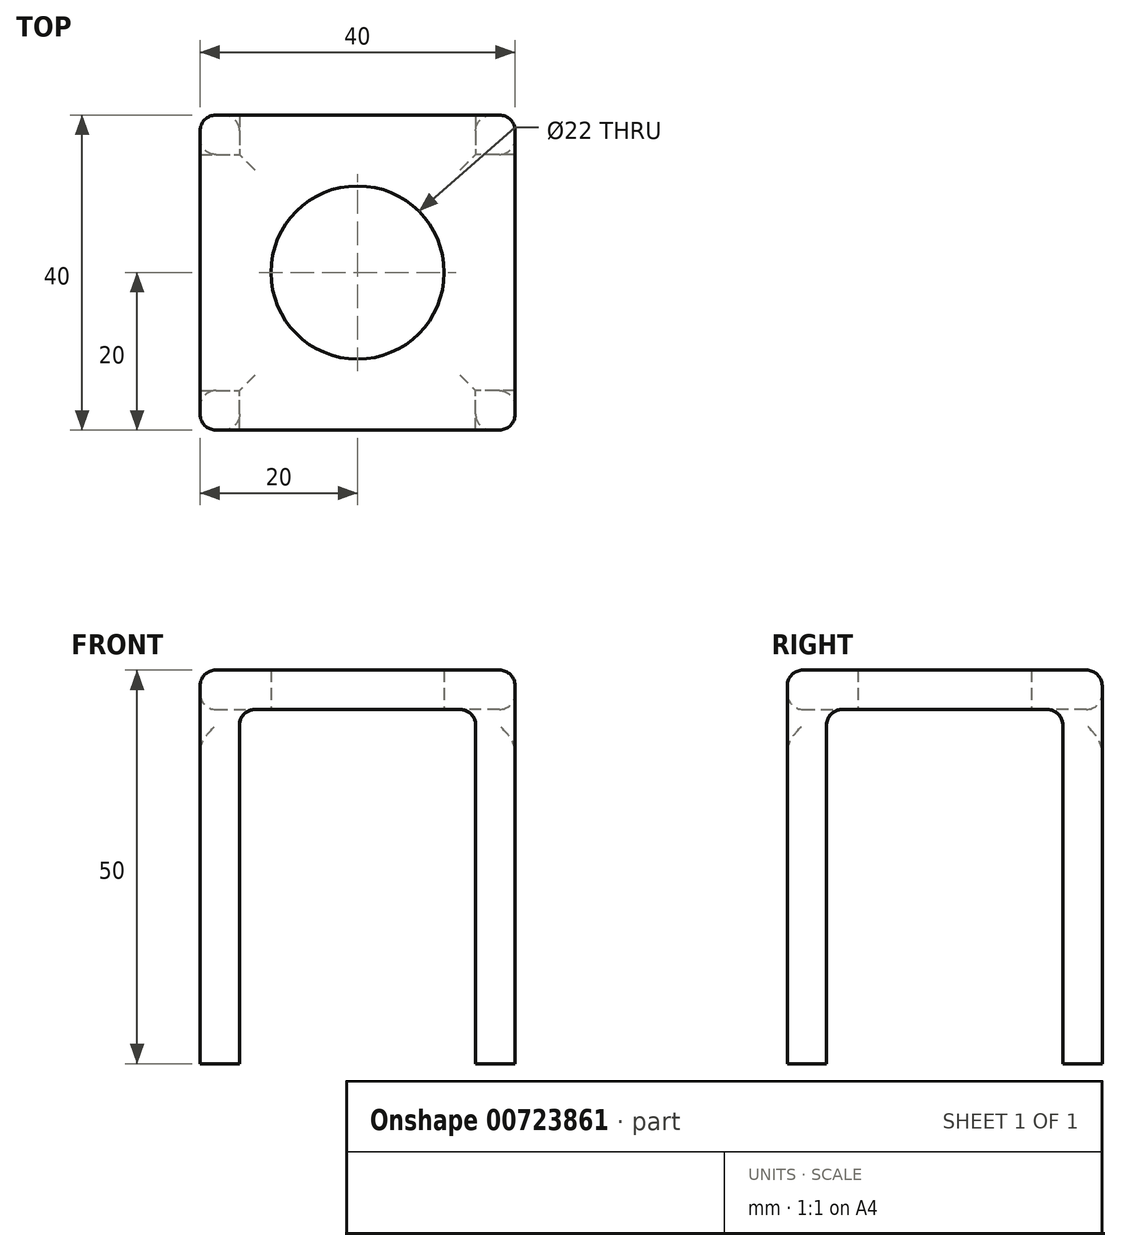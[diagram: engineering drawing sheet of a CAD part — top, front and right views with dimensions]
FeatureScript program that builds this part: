
annotation { "Feature Type Name" : "Feature", "Feature Type Description" : "" }
export const myFeature = defineFeature(function(context is Context, id is Id, definition is map)
    precondition{}
    {
        {
            var Q0;
            Q0=qCreatedBy(makeId("Top.planeOp"),FACE);
            var sketch = newSketch(context, id + "F0", { "sketchPlane" : qUnion([Q0])});
            skLineSegment(sketch, "E0.bottom", {"start": v(0, 0) * mm, "end": v(5, 0) * mm});
            skLineSegment(sketch, "E0.top", {"start": v(0, 5) * mm, "end": v(5, 5) * mm});
            skLineSegment(sketch, "E0.left", {"start": v(0, 0) * mm, "end": v(0, 5) * mm});
            skLineSegment(sketch, "E0.right", {"start": v(5, 0) * mm, "end": v(5, 5) * mm});
            skPoint(sketch, "E1", {"position": v(20, 20) * mm});
            skLineSegment(sketch, "E2.1.0", {"start": v(40, 5) * mm, "end": v(35, 5) * mm});
            skLineSegment(sketch, "E2.1.1", {"start": v(40, 0) * mm, "end": v(35, 0) * mm});
            skLineSegment(sketch, "E2.1.2", {"start": v(35, 0) * mm, "end": v(35, 5) * mm});
            skLineSegment(sketch, "E2.1.3", {"start": v(40, 0) * mm, "end": v(40, 5) * mm});
            skLineSegment(sketch, "E2.2.0", {"start": v(35, 40) * mm, "end": v(35, 35) * mm});
            skLineSegment(sketch, "E2.2.1", {"start": v(40, 40) * mm, "end": v(40, 35) * mm});
            skLineSegment(sketch, "E2.2.2", {"start": v(40, 35) * mm, "end": v(35, 35) * mm});
            skLineSegment(sketch, "E2.2.3", {"start": v(40, 40) * mm, "end": v(35, 40) * mm});
            skLineSegment(sketch, "E2.3.0", {"start": v(0, 35) * mm, "end": v(5, 35) * mm});
            skLineSegment(sketch, "E2.3.1", {"start": v(0, 40) * mm, "end": v(5, 40) * mm});
            skLineSegment(sketch, "E2.3.2", {"start": v(5, 40) * mm, "end": v(5, 35) * mm});
            skLineSegment(sketch, "E2.3.3", {"start": v(0, 40) * mm, "end": v(0, 35) * mm});
            skSolve(sketch);
        }
        {
            var Q0;
            Q0 = qSketchRegion(id + "F0", true);
            extrude(context, id + "F1", {"entities" : qUnion([Q0]), "depth" : 50 * mm, "offsetDistance" : 25 * mm});
        }
        {
            var Q0;
            Q0=makeQuery(id+"F1.opExtrude","CAP_FACE",FACE,{"disambiguationData":[OSD([sQuery(id+"F0.wireOp",EDGE,"E2.3.0"),sQuery(id+"F0.wireOp",EDGE,"E2.3.1"),sQuery(id+"F0.wireOp",EDGE,"E2.3.2"),sQuery(id+"F0.wireOp",EDGE,"E2.3.3")])],"isStart":false});
            var sketch = newSketch(context, id + "F2", { "sketchPlane" : qUnion([Q0])});
            skLineSegment(sketch, "E3.bottom", {"start": v(0, 0) * mm, "end": v(40, 0) * mm});
            skLineSegment(sketch, "E3.top", {"start": v(0, 40) * mm, "end": v(40, 40) * mm});
            skLineSegment(sketch, "E3.left", {"start": v(0, 0) * mm, "end": v(0, 40) * mm});
            skLineSegment(sketch, "E3.right", {"start": v(40, 0) * mm, "end": v(40, 40) * mm});
            skSolve(sketch);
        }
        {
            var Q0;
            Q0 = qSketchRegion(id + "F2", true);
            extrude(context, id + "F3", {"entities" : qUnion([Q0]), "operationType" : NewBodyOperationType.ADD, "oppositeDirection" : true, "depth" : 5 * mm, "offsetDistance" : 25 * mm});
        }
        {
            var Q0;
            Q0=makeQuery(id+"F3.boolean.opBoolean","MERGE",FACE,{"derivedFrom":[makeQuery(id+"F1.opExtrude","CAP_FACE",FACE,{"disambiguationData":[OSD([sQuery(id+"F0.wireOp",EDGE,"E0.bottom"),sQuery(id+"F0.wireOp",EDGE,"E0.top"),sQuery(id+"F0.wireOp",EDGE,"E0.left"),sQuery(id+"F0.wireOp",EDGE,"E0.right")])],"isStart":false}),makeQuery(id+"F1.opExtrude","CAP_FACE",FACE,{"disambiguationData":[OSD([sQuery(id+"F0.wireOp",EDGE,"E2.1.0"),sQuery(id+"F0.wireOp",EDGE,"E2.1.1"),sQuery(id+"F0.wireOp",EDGE,"E2.1.2"),sQuery(id+"F0.wireOp",EDGE,"E2.1.3")])],"isStart":false}),makeQuery(id+"F1.opExtrude","CAP_FACE",FACE,{"disambiguationData":[OSD([sQuery(id+"F0.wireOp",EDGE,"E2.2.0"),sQuery(id+"F0.wireOp",EDGE,"E2.2.1"),sQuery(id+"F0.wireOp",EDGE,"E2.2.2"),sQuery(id+"F0.wireOp",EDGE,"E2.2.3")])],"isStart":false}),makeQuery(id+"F1.opExtrude","CAP_FACE",FACE,{"disambiguationData":[OSD([sQuery(id+"F0.wireOp",EDGE,"E2.3.0"),sQuery(id+"F0.wireOp",EDGE,"E2.3.1"),sQuery(id+"F0.wireOp",EDGE,"E2.3.2"),sQuery(id+"F0.wireOp",EDGE,"E2.3.3")])],"isStart":false}),makeQuery(id+"F3.opExtrude","CAP_FACE",FACE,{"disambiguationData":[OSD([sQuery(id+"F2.wireOp",EDGE,"E3.bottom"),sQuery(id+"F2.wireOp",EDGE,"E3.top"),sQuery(id+"F2.wireOp",EDGE,"E3.left"),sQuery(id+"F2.wireOp",EDGE,"E3.right")])],"isStart":true})]});
            var Q1;
            Q1=makeQuery(id+"F1.opExtrude","SWEPT_EDGE",EDGE,{"disambiguationData":[OSD([sQuery(id+"F0.wireOp",EDGE,"E0.bottom"),sQuery(id+"F0.wireOp",EDGE,"E0.left")])]});
            var Q2;
            Q2=makeQuery(id+"F1.opExtrude","SWEPT_EDGE",EDGE,{"disambiguationData":[OSD([sQuery(id+"F0.wireOp",EDGE,"E2.1.1"),sQuery(id+"F0.wireOp",EDGE,"E2.1.3")])]});
            var Q3;
            Q3=makeQuery(id+"F1.opExtrude","SWEPT_EDGE",EDGE,{"disambiguationData":[OSD([sQuery(id+"F0.wireOp",EDGE,"E2.2.1"),sQuery(id+"F0.wireOp",EDGE,"E2.2.3")])]});
            var Q4;
            Q4=makeQuery(id+"F3.opExtrude","CAP_FACE",FACE,{"disambiguationData":[OSD([sQuery(id+"F2.wireOp",EDGE,"E3.bottom"),sQuery(id+"F2.wireOp",EDGE,"E3.top"),sQuery(id+"F2.wireOp",EDGE,"E3.left"),sQuery(id+"F2.wireOp",EDGE,"E3.right")])],"isStart":false});
            var Q5;
            Q5=makeQuery(id+"F1.opExtrude","SWEPT_EDGE",EDGE,{"disambiguationData":[OSD([sQuery(id+"F0.wireOp",EDGE,"E2.3.1"),sQuery(id+"F0.wireOp",EDGE,"E2.3.3")])]});
            fillet(context, id + "F4", {"entities" : qUnion([Q0, Q1, Q2, Q3, Q4, Q5]), "radius" : 2 * mm, "tangentPropagation" : true, "allowEdgeOverflow" : false});
        }
        {
            var Q0;
            Q0=sQuery(id+"F0.wireOp",VERTEX,"E1");
            var Q1;
            Q1=makeQuery(id+"F1.opExtrude","SWEPT_BODY",BODY,{"disambiguationData":[OSD([sQuery(id+"F0.wireOp",EDGE,"E0.bottom"),sQuery(id+"F0.wireOp",EDGE,"E0.top"),sQuery(id+"F0.wireOp",EDGE,"E0.left"),sQuery(id+"F0.wireOp",EDGE,"E0.right")])]});
            hole(context, id + "F5", {"style" : HoleStyle.SIMPLE, "endStyle" : HoleEndStyle.BLIND, "oppositeDirection" : true, "standardTappedOrClearance" : lookupTablePath({ "standard" : "ISO", "fit" : "Normal", "size" : "M20", "type" : "Clearance" }), "standardBlindInLast" : lookupTablePath({ "fit" : "Standard", "standard" : "ISO", "size" : "M20", "type" : "Clearance" }), "holeDiameter" : 22 * mm, "majorDiameter" : 5 * mm, "holeDepth" : 50 * mm, "tappedDepth" : 5 * mm, "tapClearance" : 0, "locations" : qUnion([Q0]), "scope" : qUnion([Q1])});
        }
    });
